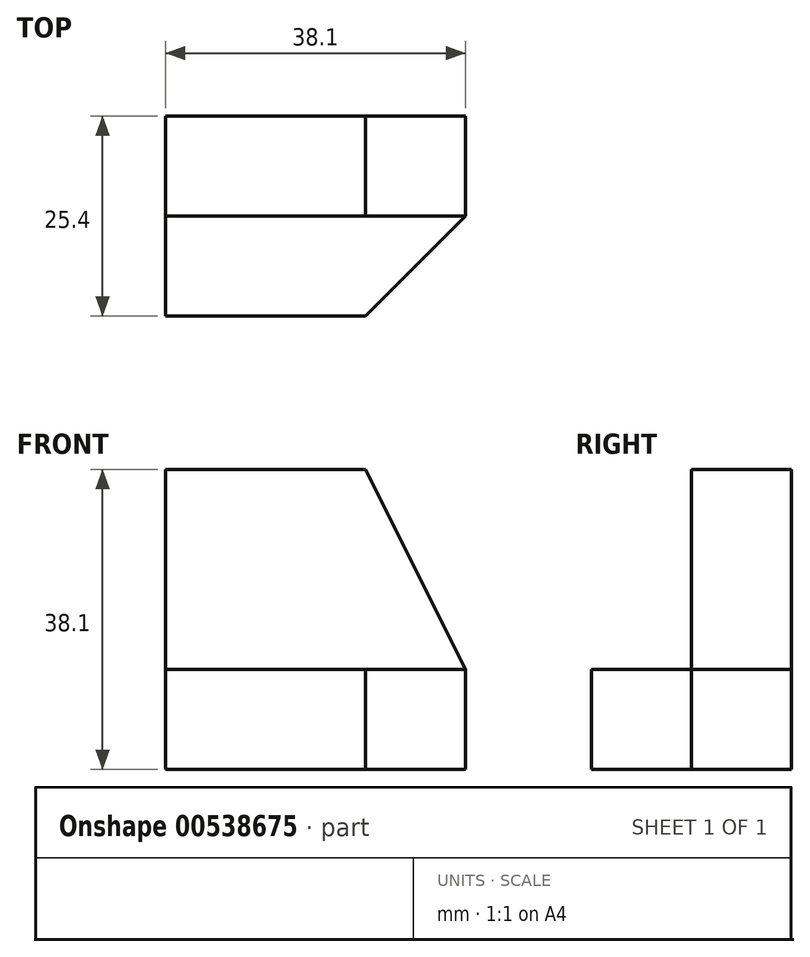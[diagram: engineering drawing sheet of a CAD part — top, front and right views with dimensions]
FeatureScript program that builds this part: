
annotation { "Feature Type Name" : "Feature", "Feature Type Description" : "" }
export const myFeature = defineFeature(function(context is Context, id is Id, definition is map)
    precondition{}
    {
        {
            var Q0;
            Q0=qCreatedBy(makeId("Right.planeOp"),FACE);
            var sketch = newSketch(context, id + "F0", { "sketchPlane" : qUnion([Q0])});
            skLineSegment(sketch, "E0", {"start": v(-12.28, 43.3) * mm, "end": v(-24.98, 43.3) * mm});
            skLineSegment(sketch, "E1", {"start": v(-24.98, 43.3) * mm, "end": v(-24.98, 17.9) * mm});
            skLineSegment(sketch, "E2", {"start": v(-24.98, 17.9) * mm, "end": v(-37.68, 17.9) * mm});
            skLineSegment(sketch, "E3", {"start": v(-37.68, 17.9) * mm, "end": v(-37.68, 5.2) * mm});
            skLineSegment(sketch, "E4", {"start": v(-37.68, 5.2) * mm, "end": v(-12.28, 5.2) * mm});
            skLineSegment(sketch, "E5", {"start": v(-12.28, 5.2) * mm, "end": v(-12.28, 43.3) * mm});
            skSolve(sketch);
        }
        {
            var Q0;
            Q0=makeQuery(id+"F0.imprint","IMPRINT",FACE,{"disambiguationData":[TD([[makeQuery(id+"F0.imprint","IMPRINT",EDGE,{"derivedFrom":sQuery(id+"F0.wireOp",EDGE,"E0")}),1.0]])]});
            extrude(context, id + "F1", {"entities" : qUnion([Q0]), "depth" : 38.1 * mm, "offsetDistance" : 25.4 * mm});
        }
        {
            var Q0;
            Q0=makeQuery(id+"F1.opExtrude","SWEPT_FACE",FACE,{"disambiguationData":[OSD([sQuery(id+"F0.wireOp",EDGE,"E1")])]});
            var sketch = newSketch(context, id + "F2", { "sketchPlane" : qUnion([Q0])});
            skLineSegment(sketch, "E6", {"start": v(25.4, 43.3) * mm, "end": v(38.1, 17.9) * mm});
            skLineSegment(sketch, "E7", {"start": v(38.1, 17.9) * mm, "end": v(25.4, 5.36) * mm});
            skSolve(sketch);
        }
        {
            var Q0;
            {var subQ0=sQuery(id+"F2.wireOp",EDGE,"E6");Q0=makeQuery(id+"F2.imprint","IMPRINT",FACE,{"disambiguationData":[TD([[makeQuery(id+"F2.imprint","IMPRINT",EDGE,{"derivedFrom":subQ0}),1.0]])]});}
            extrude(context, id + "F3", {"entities" : qUnion([Q0]), "operationType" : NewBodyOperationType.REMOVE, "oppositeDirection" : true, "depth" : 25.4 * mm, "offsetDistance" : 25.4 * mm});
        }
        {
            var Q0;
            Q0=makeQuery(id+"F1.opExtrude","SWEPT_FACE",FACE,{"disambiguationData":[OSD([sQuery(id+"F0.wireOp",EDGE,"E2")])]});
            var sketch = newSketch(context, id + "F4", { "sketchPlane" : qUnion([Q0])});
            skLineSegment(sketch, "E8", {"start": v(38.1, -24.98) * mm, "end": v(25.4, -37.68) * mm});
            skSolve(sketch);
        }
        {
            var Q0;
            {var subQ0=sQuery(id+"F4.wireOp",EDGE,"E8");Q0=makeQuery(id+"F4.imprint","IMPRINT",FACE,{"disambiguationData":[TD([[makeQuery(id+"F4.imprint","IMPRINT",EDGE,{"derivedFrom":subQ0}),1.0]])]});}
            extrude(context, id + "F5", {"entities" : qUnion([Q0]), "operationType" : NewBodyOperationType.REMOVE, "oppositeDirection" : true, "depth" : 25.4 * mm, "offsetDistance" : 25.4 * mm});
        }
    });
